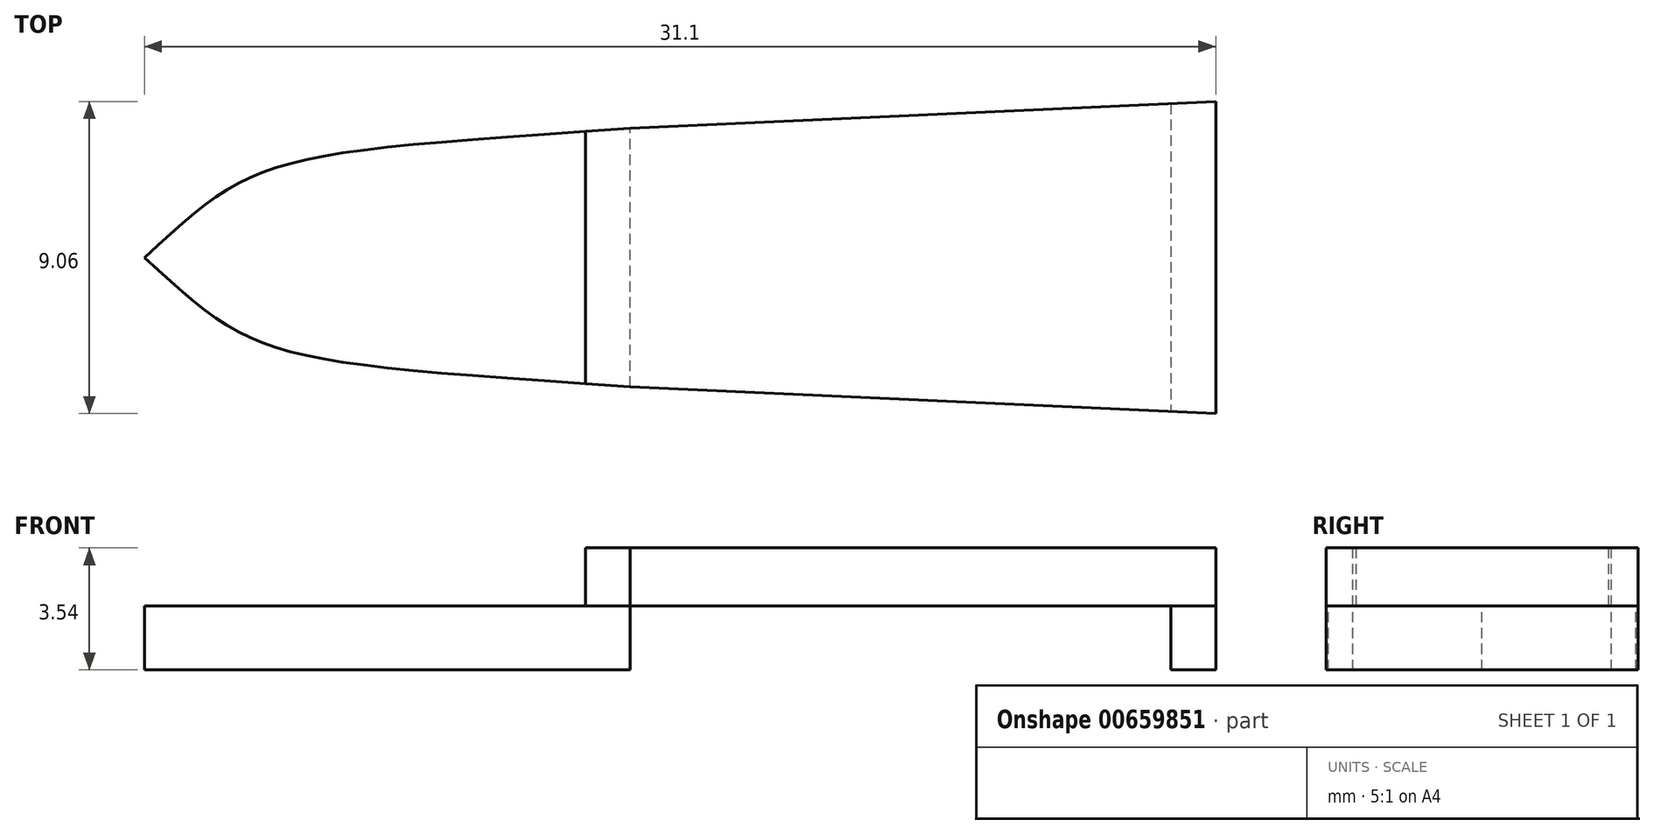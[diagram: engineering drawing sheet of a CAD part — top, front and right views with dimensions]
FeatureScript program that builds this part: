
annotation { "Feature Type Name" : "Feature", "Feature Type Description" : "" }
export const myFeature = defineFeature(function(context is Context, id is Id, definition is map)
    precondition{}
    {
        {
            var Q0;
            Q0=qCreatedBy(makeId("Top.planeOp"),FACE);
            var sketch = newSketch(context, id + "F0", { "sketchPlane" : qUnion([Q0])});
            skLineSegment(sketch, "E0", {"start": v(-9.5, 0) * mm, "end": v(-10.8, 0) * mm});
            skLineSegment(sketch, "E1", {"start": v(-10.8, 0) * mm, "end": v(-26.5, 0) * mm});
            skLineSegment(sketch, "E2", {"start": v(-26.5, 0) * mm, "end": v(-27.8, 0) * mm});
            skLineSegment(sketch, "E3", {"start": v(-27.8, 0) * mm, "end": v(-40.6, 0) * mm});
            skLineSegment(sketch, "E4", {"start": v(0, 0) * mm, "end": v(0, 4.53) * mm});
            skLineSegment(sketch, "E5", {"start": v(0, 4.53) * mm, "end": v(0, 0) * mm});
            skLineSegment(sketch, "E6", {"start": v(0, 0) * mm, "end": v(0, -4.53) * mm});
            skLineSegment(sketch, "E7", {"start": v(-9.5, 0) * mm, "end": v(-9.5, 4.53) * mm});
            skLineSegment(sketch, "E8", {"start": v(-9.5, 4.53) * mm, "end": v(0, 4.53) * mm});
            skLineSegment(sketch, "E9", {"start": v(-9.5, 0) * mm, "end": v(-9.5, -4.53) * mm});
            skLineSegment(sketch, "E10", {"start": v(-9.5, -4.53) * mm, "end": v(0, -4.53) * mm});
            skLineSegment(sketch, "E11", {"start": v(-26.5, 0) * mm, "end": v(-26.5, 3.75) * mm});
            skLineSegment(sketch, "E12", {"start": v(-26.5, 3.75) * mm, "end": v(-9.5, 4.52) * mm});
            skLineSegment(sketch, "E13", {"start": v(-26.5, 0) * mm, "end": v(-26.5, -3.75) * mm});
            skLineSegment(sketch, "E14", {"start": v(-26.5, -3.75) * mm, "end": v(-9.5, -4.52) * mm});
            skLineSegment(sketch, "E15", {"start": v(-10.8, 0) * mm, "end": v(-10.8, 4.47) * mm});
            skLineSegment(sketch, "E16", {"start": v(-10.8, 0) * mm, "end": v(-10.8, -4.47) * mm});
            skFitSpline(sketch, "E17", {"points": [v(-40.6, 0) * mm, v(-26.5, 3.75) * mm], "startDerivative": vector(9.88, 9.05) * mm, "endDerivative": vector(32.42, 2.2) * mm});
            skFitSpline(sketch, "E18.MirrorCS", {"points": [v(-40.6, 0) * mm, v(-26.5, -3.75) * mm], "startDerivative": vector(9.88, -9.05) * mm, "endDerivative": vector(32.42, -2.2) * mm});
            skLineSegment(sketch, "E19", {"start": v(-27.8, 0) * mm, "end": v(-27.8, 3.66) * mm});
            skLineSegment(sketch, "E20", {"start": v(-27.8, 0) * mm, "end": v(-27.8, -3.66) * mm});
            skSolve(sketch);
        }
        {
            var Q0;
            Q0=makeQuery(id+"F0.imprint","IMPRINT",FACE,{"disambiguationData":[TD([[makeQuery(id+"F0.imprint","IMPRINT",EDGE,{"derivedFrom":sQuery(id+"F0.wireOp",EDGE,"E5")}),-1.0]])]});
            var Q1;
            Q1=makeQuery(id+"F0.imprint","IMPRINT",FACE,{"disambiguationData":[TD([[makeQuery(id+"F0.imprint","IMPRINT",EDGE,{"derivedFrom":sQuery(id+"F0.wireOp",EDGE,"E0")}),1.0]])]});
            var Q2;
            Q2=makeQuery(id+"F0.imprint","IMPRINT",FACE,{"disambiguationData":[TD([[makeQuery(id+"F0.imprint","IMPRINT",EDGE,{"derivedFrom":sQuery(id+"F0.wireOp",EDGE,"E2")}),-1.0]])]});
            var Q3;
            Q3=makeQuery(id+"F0.imprint","IMPRINT",FACE,{"disambiguationData":[TD([[makeQuery(id+"F0.imprint","IMPRINT",EDGE,{"derivedFrom":sQuery(id+"F0.wireOp",EDGE,"E2")}),1.0]])]});
            var Q4;
            {var subQ0=sQuery(id+"F0.wireOp",EDGE,"E3");Q4=makeQuery(id+"F0.imprint","IMPRINT",FACE,{"disambiguationData":[TD([[makeQuery(id+"F0.imprint","IMPRINT",EDGE,{"derivedFrom":subQ0}),1.0]])]});}
            var Q5;
            {var subQ0=sQuery(id+"F0.wireOp",EDGE,"E3");Q5=makeQuery(id+"F0.imprint","IMPRINT",FACE,{"disambiguationData":[TD([[makeQuery(id+"F0.imprint","IMPRINT",EDGE,{"derivedFrom":subQ0}),-1.0]])]});}
            var Q6;
            Q6=makeQuery(id+"F0.imprint","IMPRINT",FACE,{"disambiguationData":[TD([[makeQuery(id+"F0.imprint","IMPRINT",EDGE,{"derivedFrom":sQuery(id+"F0.wireOp",EDGE,"E0")}),-1.0]])]});
            extrude(context, id + "F1", {"entities" : qUnion([Q0, Q1, Q2, Q3, Q4, Q5, Q6]), "depth" : -1.86 * mm, "offsetDistance" : 25 * mm});
        }
        {
            var Q0;
            Q0=makeQuery(id+"F0.imprint","IMPRINT",FACE,{"disambiguationData":[TD([[makeQuery(id+"F0.imprint","IMPRINT",EDGE,{"derivedFrom":sQuery(id+"F0.wireOp",EDGE,"E2")}),-1.0]])]});
            var Q1;
            Q1=makeQuery(id+"F0.imprint","IMPRINT",FACE,{"disambiguationData":[TD([[makeQuery(id+"F0.imprint","IMPRINT",EDGE,{"derivedFrom":sQuery(id+"F0.wireOp",EDGE,"E2")}),1.0]])]});
            var Q2;
            Q2=makeQuery(id+"F0.imprint","IMPRINT",FACE,{"disambiguationData":[TD([[makeQuery(id+"F0.imprint","IMPRINT",EDGE,{"derivedFrom":sQuery(id+"F0.wireOp",EDGE,"E1")}),1.0]])]});
            var Q3;
            Q3=makeQuery(id+"F0.imprint","IMPRINT",FACE,{"disambiguationData":[TD([[makeQuery(id+"F0.imprint","IMPRINT",EDGE,{"derivedFrom":sQuery(id+"F0.wireOp",EDGE,"E1")}),-1.0]])]});
            var Q4;
            Q4=makeQuery(id+"F0.imprint","IMPRINT",FACE,{"disambiguationData":[TD([[makeQuery(id+"F0.imprint","IMPRINT",EDGE,{"derivedFrom":sQuery(id+"F0.wireOp",EDGE,"E0")}),-1.0]])]});
            var Q5;
            Q5=makeQuery(id+"F0.imprint","IMPRINT",FACE,{"disambiguationData":[TD([[makeQuery(id+"F0.imprint","IMPRINT",EDGE,{"derivedFrom":sQuery(id+"F0.wireOp",EDGE,"E0")}),1.0]])]});
            extrude(context, id + "F2", {"entities" : qUnion([Q0, Q1, Q2, Q3, Q4, Q5]), "depth" : 1.68 * mm, "offsetDistance" : 25 * mm});
        }
    });
